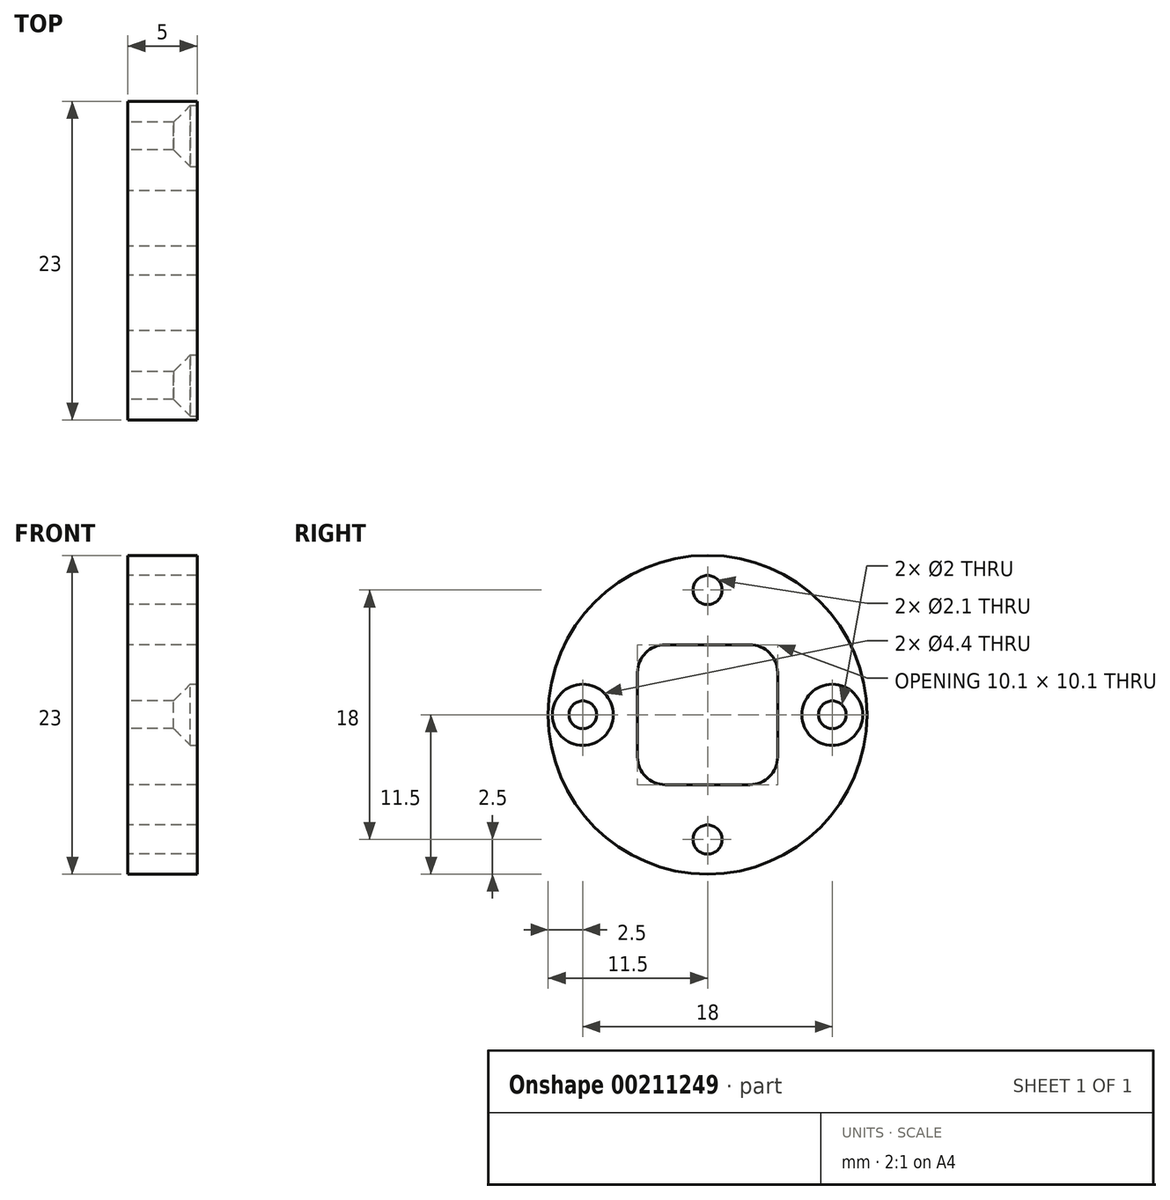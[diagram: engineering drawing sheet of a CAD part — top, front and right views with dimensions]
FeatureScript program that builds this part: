
annotation { "Feature Type Name" : "Feature", "Feature Type Description" : "" }
export const myFeature = defineFeature(function(context is Context, id is Id, definition is map)
    precondition{}
    {
        {
            var Q0;
            Q0=qCreatedBy(makeId("Right.planeOp"),FACE);
            var sketch = newSketch(context, id + "F0", { "sketchPlane" : qUnion([Q0])});
            skCircle(sketch, "E0", {"center": v(0, 0) * mm, "radius": 11.5 * mm});
            skCircle(sketch, "E1", {"center": v(0, 0) * mm, "radius": 9 * mm, "construction": true});
            skCircle(sketch, "E2", {"center": v(0, 9) * mm, "radius": 1.05 * mm});
            skCircle(sketch, "E3", {"center": v(9, 0) * mm, "radius": 1 * mm});
            skCircle(sketch, "E4", {"center": v(0, -9) * mm, "radius": 1.05 * mm});
            skCircle(sketch, "E5", {"center": v(-9, 0) * mm, "radius": 1 * mm});
            skLineSegment(sketch, "E6.bottom", {"start": v(-2, 3) * mm, "end": v(2, 3) * mm, "construction": true});
            skLineSegment(sketch, "E6.top", {"start": v(-2, -3) * mm, "end": v(2, -3) * mm, "construction": true});
            skLineSegment(sketch, "E6.left", {"start": v(-3, 2) * mm, "end": v(-3, -2) * mm, "construction": true});
            skLineSegment(sketch, "E6.right", {"start": v(3, 2) * mm, "end": v(3, -2) * mm, "construction": true});
            skArc(sketch, "E7", {"start": v(-3.05, 5.05) * mm, "mid": v(-4.46, 4.46) * mm, "end": v(-5.05, 3.05) * mm});
            skArc(sketch, "E8", {"start": v(-5.05, -3.05) * mm, "mid": v(-4.46, -4.46) * mm, "end": v(-3.05, -5.05) * mm});
            skArc(sketch, "E9", {"start": v(3.05, -5.05) * mm, "mid": v(4.46, -4.46) * mm, "end": v(5.05, -3.05) * mm});
            skArc(sketch, "E10", {"start": v(5.05, 3.05) * mm, "mid": v(4.46, 4.46) * mm, "end": v(3.05, 5.05) * mm});
            skLineSegment(sketch, "E11", {"start": v(-5.05, 3.05) * mm, "end": v(-5.05, -3.05) * mm});
            skLineSegment(sketch, "E12", {"start": v(-3.05, -5.05) * mm, "end": v(3.05, -5.05) * mm});
            skLineSegment(sketch, "E13", {"start": v(5.05, -3.05) * mm, "end": v(5.05, 3.05) * mm});
            skLineSegment(sketch, "E14", {"start": v(-3.05, 5.05) * mm, "end": v(3.05, 5.05) * mm});
            skLineSegment(sketch, "E15.bottom", {"start": v(4.4, -4.4) * mm, "end": v(-4.4, -4.4) * mm, "construction": true});
            skLineSegment(sketch, "E15.top", {"start": v(4.4, 4.4) * mm, "end": v(-4.4, 4.4) * mm, "construction": true});
            skLineSegment(sketch, "E15.left", {"start": v(4.4, -4.4) * mm, "end": v(4.4, 4.4) * mm, "construction": true});
            skLineSegment(sketch, "E15.right", {"start": v(-4.4, -4.4) * mm, "end": v(-4.4, 4.4) * mm, "construction": true});
            skArc(sketch, "E16", {"start": v(-3, -2) * mm, "mid": v(-2.7, -2.7) * mm, "end": v(-2, -3) * mm, "construction": true});
            skArc(sketch, "E17", {"start": v(2, -3) * mm, "mid": v(2.7, -2.7) * mm, "end": v(3, -2) * mm, "construction": true});
            skArc(sketch, "E18", {"start": v(3, 2) * mm, "mid": v(2.7, 2.7) * mm, "end": v(2, 3) * mm, "construction": true});
            skArc(sketch, "E19", {"start": v(-2, 3) * mm, "mid": v(-2.7, 2.7) * mm, "end": v(-3, 2) * mm, "construction": true});
            skSolve(sketch);
        }
        {
            var Q0;
            Q0=qSketchRegion(id+"F0",true);
            extrude(context, id + "F1", {"entities" : qUnion([Q0]), "offsetDistance" : 25 * mm, "depth" : 5 * mm});
        }
        {
            var Q0;
            Q0=qCreatedBy(makeId("Front.planeOp"),FACE);
            cPlane(context, id + "F2", {"entities" : qUnion([Q0]), "cplaneType" : CPlaneType.OFFSET, "offset" : 9 * mm, "width" : 150 * mm, "height" : 150 * mm});
        }
        {
            var Q0;
            Q0=qCreatedBy(id+"F2.planeOp",FACE);
            var sketch = newSketch(context, id + "F3", { "sketchPlane" : qUnion([Q0])});
            skLineSegment(sketch, "E20", {"start": v(5, 0) * mm, "end": v(2.3, 0) * mm});
            skLineSegment(sketch, "E21", {"start": v(2.3, 0) * mm, "end": v(4.5, 2.2) * mm});
            skLineSegment(sketch, "E22", {"start": v(4.5, 2.2) * mm, "end": v(5, 2.2) * mm});
            skLineSegment(sketch, "E23", {"start": v(5, 2.2) * mm, "end": v(5, 0) * mm});
            skSolve(sketch);
        }
        {
            var Q0;
            Q0=qCreatedBy(id+"F2.planeOp",FACE);
            var sketch = newSketch(context, id + "F4", { "sketchPlane" : qUnion([Q0])});
            skLineSegment(sketch, "E24", {"start": v(-0.83, 0) * mm, "end": v(6.33, 0) * mm});
            skSolve(sketch);
        }
        {
            var Q0;
            Q0=qSketchRegion(id+"F3",true);
            var Q1;
            Q1=sQuery(id+"F4.wireOp",EDGE,"E24");
            revolve(context, id + "F5", {"operationType" : NewBodyOperationType.REMOVE, "entities" : qUnion([Q0]), "axis" : qUnion([Q1]), "revolveType" : RevolveType.FULL, "oppositeDirection" : true});
        }
        {
            var Q0;
            Q0=qCreatedBy(makeId("Front.planeOp"),FACE);
            cPlane(context, id + "F6", {"entities" : qUnion([Q0]), "cplaneType" : CPlaneType.OFFSET, "offset" : 9 * mm, "oppositeDirection" : true, "width" : 150 * mm, "height" : 150 * mm});
        }
        {
            var Q0;
            Q0=qCreatedBy(id+"F6.planeOp",FACE);
            var sketch = newSketch(context, id + "F7", { "sketchPlane" : qUnion([Q0])});
            skLineSegment(sketch, "E25", {"start": v(2.3, 0) * mm, "end": v(5, 0) * mm});
            skLineSegment(sketch, "E26", {"start": v(5, 0) * mm, "end": v(5, 2.2) * mm});
            skLineSegment(sketch, "E27", {"start": v(5, 2.2) * mm, "end": v(4.5, 2.2) * mm});
            skLineSegment(sketch, "E28", {"start": v(4.5, 2.2) * mm, "end": v(2.3, 0) * mm});
            skSolve(sketch);
        }
        {
            var Q0;
            Q0=qSketchRegion(id+"F7",true);
            var Q1;
            Q1=sQuery(id+"F7.wireOp",EDGE,"E25");
            revolve(context, id + "F8", {"operationType" : NewBodyOperationType.REMOVE, "entities" : qUnion([Q0]), "axis" : qUnion([Q1]), "revolveType" : RevolveType.FULL, "oppositeDirection" : true});
        }
    });
